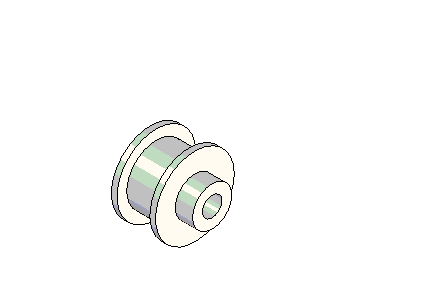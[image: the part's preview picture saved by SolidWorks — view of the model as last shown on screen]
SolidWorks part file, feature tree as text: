
SOLIDWORKS PART (.sldprt)
format: sldprt  version: not decoded by parser v0  size: 139,264 bytes
history: native  units: mm
features: sketch x5, extrude x4, cut_extrude x1 (+11 scaffold rows collapsed)
feature tree (21):
  scaffold x11  (default folders/planes/origin — collapsed)
  sketch  "Sketch1"  dims[D1=12.7mm]
  extrude  "Extrude1"  Depth=5.55625mm
  sketch  "Sketch2"  dims[D1=25.4mm]
  extrude  "Extrude2"  Depth=1.83515mm
  sketch  "Sketch3"  dims[D1=19.05mm]
  extrude  "Extrude3"  Depth=10.6172mm
  sketch  "Sketch4"
  extrude  "Extrude4"  Depth=1.83515mm
  sketch  "Sketch5"  dims[D1=6.35mm]
  cut_extrude  "Cut-Extrude1"  [1 undecoded]
decode coverage: 8 of 10 modeling features carry decoded parameters
note: 1 parameter value undecoded
note: suppression state not decoded; provenance and decode notes live in map.json
